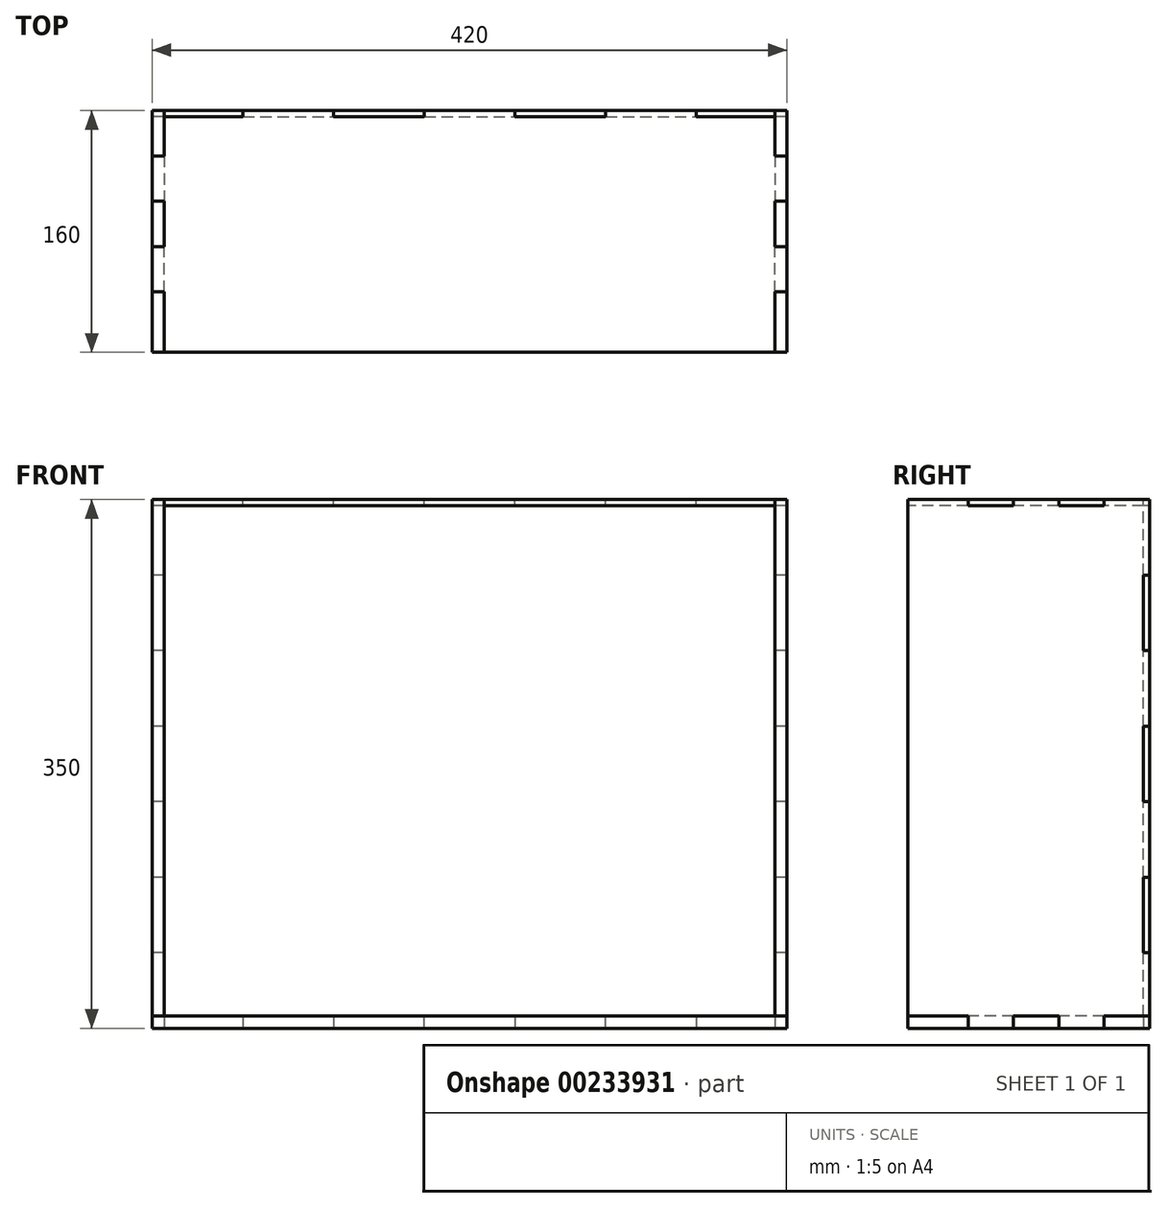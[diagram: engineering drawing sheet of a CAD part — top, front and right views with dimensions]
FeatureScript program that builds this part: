
annotation { "Feature Type Name" : "Feature", "Feature Type Description" : "" }
export const myFeature = defineFeature(function(context is Context, id is Id, definition is map)
    precondition{}
    {
        {
            var Q0;
            Q0=qCreatedBy(makeId("Top.planeOp"),FACE);
            var sketch = newSketch(context, id + "F0", { "sketchPlane" : qUnion([Q0])});
            skLineSegment(sketch, "E0", {"start": v(0, 0) * mm, "end": v(0, 40) * mm});
            skLineSegment(sketch, "E1", {"start": v(0, 40) * mm, "end": v(8, 40) * mm});
            skLineSegment(sketch, "E2", {"start": v(8, 40) * mm, "end": v(8, 70) * mm});
            skLineSegment(sketch, "E3", {"start": v(8, 70) * mm, "end": v(0, 70) * mm});
            skLineSegment(sketch, "E4", {"start": v(0, 70) * mm, "end": v(0, 100) * mm});
            skLineSegment(sketch, "E5", {"start": v(0, 100) * mm, "end": v(8, 100) * mm});
            skLineSegment(sketch, "E6", {"start": v(8, 100) * mm, "end": v(8, 130) * mm});
            skLineSegment(sketch, "E7", {"start": v(8, 130) * mm, "end": v(0, 130) * mm});
            skLineSegment(sketch, "E8", {"start": v(0, 130) * mm, "end": v(0, 160) * mm});
            skLineSegment(sketch, "E9", {"start": v(0, 160) * mm, "end": v(60, 160) * mm});
            skLineSegment(sketch, "E10", {"start": v(60, 160) * mm, "end": v(60, 156) * mm});
            skLineSegment(sketch, "E11", {"start": v(60, 156) * mm, "end": v(120, 156) * mm});
            skLineSegment(sketch, "E12", {"start": v(120, 156) * mm, "end": v(120, 160) * mm});
            skLineSegment(sketch, "E13", {"start": v(120, 160) * mm, "end": v(180, 160) * mm});
            skLineSegment(sketch, "E14", {"start": v(180, 160) * mm, "end": v(180, 156) * mm});
            skLineSegment(sketch, "E15", {"start": v(180, 156) * mm, "end": v(240, 156) * mm});
            skLineSegment(sketch, "E16", {"start": v(240, 156) * mm, "end": v(240, 160) * mm});
            skLineSegment(sketch, "E17", {"start": v(240, 160) * mm, "end": v(300, 160) * mm});
            skLineSegment(sketch, "E18", {"start": v(300, 160) * mm, "end": v(300, 156) * mm});
            skLineSegment(sketch, "E19", {"start": v(300, 156) * mm, "end": v(360, 156) * mm});
            skLineSegment(sketch, "E20", {"start": v(360, 156) * mm, "end": v(360, 160) * mm});
            skLineSegment(sketch, "E21", {"start": v(360, 160) * mm, "end": v(420, 160) * mm});
            skLineSegment(sketch, "E22", {"start": v(420, 160) * mm, "end": v(420, 130) * mm});
            skLineSegment(sketch, "E23", {"start": v(420, 130) * mm, "end": v(412, 130) * mm});
            skLineSegment(sketch, "E24", {"start": v(412, 130) * mm, "end": v(412, 100) * mm});
            skLineSegment(sketch, "E25", {"start": v(412, 100) * mm, "end": v(420, 100) * mm});
            skLineSegment(sketch, "E26", {"start": v(420, 100) * mm, "end": v(420, 70) * mm});
            skLineSegment(sketch, "E27", {"start": v(420, 70) * mm, "end": v(412, 70) * mm});
            skLineSegment(sketch, "E28", {"start": v(412, 70) * mm, "end": v(412, 40) * mm});
            skLineSegment(sketch, "E29", {"start": v(412, 40) * mm, "end": v(420, 40) * mm});
            skLineSegment(sketch, "E30", {"start": v(420, 40) * mm, "end": v(420, 0) * mm});
            skLineSegment(sketch, "E31", {"start": v(420, 0) * mm, "end": v(0, 0) * mm});
            skSolve(sketch);
        }
        {
            var Q0;
            Q0=makeQuery(id+"F0.imprint","IMPRINT",FACE,{"disambiguationData":[TD([[makeQuery(id+"F0.imprint","IMPRINT",EDGE,{"derivedFrom":sQuery(id+"F0.wireOp",EDGE,"E0")}),-1.0]])]});
            extrude(context, id + "F1", {"entities" : qUnion([Q0]), "depth" : 8 * mm});
        }
        {
            var Q0;
            Q0=makeQuery(id+"F1.opExtrude","SWEPT_FACE",FACE,{"disambiguationData":[OSD([sQuery(id+"F0.wireOp",EDGE,"E0")])]});
            var sketch = newSketch(context, id + "F2", { "sketchPlane" : qUnion([Q0])});
            skLineSegment(sketch, "E32", {"start": v(0, 8) * mm, "end": v(-40, 8) * mm});
            skLineSegment(sketch, "E33", {"start": v(-40, 8) * mm, "end": v(-40, 0) * mm});
            skLineSegment(sketch, "E34", {"start": v(-40, 0) * mm, "end": v(-70, 0) * mm});
            skLineSegment(sketch, "E35", {"start": v(-70, 0) * mm, "end": v(-70, 8) * mm});
            skLineSegment(sketch, "E36", {"start": v(-70, 8) * mm, "end": v(-100, 8) * mm});
            skLineSegment(sketch, "E37", {"start": v(-100, 8) * mm, "end": v(-100, 0) * mm});
            skLineSegment(sketch, "E38", {"start": v(-100, 0) * mm, "end": v(-130, 0) * mm});
            skLineSegment(sketch, "E39", {"start": v(-130, 0) * mm, "end": v(-130, 8) * mm});
            skLineSegment(sketch, "E40", {"start": v(-130, 8) * mm, "end": v(-160, 8) * mm});
            skLineSegment(sketch, "E41", {"start": v(-160, 8) * mm, "end": v(-160, 50) * mm});
            skLineSegment(sketch, "E42", {"start": v(-160, 50) * mm, "end": v(-156, 50) * mm});
            skLineSegment(sketch, "E43", {"start": v(-156, 50) * mm, "end": v(-156, 100) * mm});
            skLineSegment(sketch, "E44", {"start": v(-156, 100) * mm, "end": v(-160, 100) * mm});
            skLineSegment(sketch, "E45", {"start": v(-160, 100) * mm, "end": v(-160, 150) * mm});
            skLineSegment(sketch, "E46", {"start": v(-160, 150) * mm, "end": v(-156, 150) * mm});
            skLineSegment(sketch, "E47", {"start": v(-156, 150) * mm, "end": v(-156, 200) * mm});
            skLineSegment(sketch, "E48", {"start": v(-156, 200) * mm, "end": v(-160, 200) * mm});
            skLineSegment(sketch, "E49", {"start": v(-160, 200) * mm, "end": v(-160, 250) * mm});
            skLineSegment(sketch, "E50", {"start": v(-160, 250) * mm, "end": v(-156, 250) * mm});
            skLineSegment(sketch, "E51", {"start": v(-156, 250) * mm, "end": v(-156, 300) * mm});
            skLineSegment(sketch, "E52", {"start": v(-156, 300) * mm, "end": v(-160, 300) * mm});
            skLineSegment(sketch, "E53", {"start": v(-160, 300) * mm, "end": v(-160, 350) * mm});
            skLineSegment(sketch, "E54", {"start": v(-160, 350) * mm, "end": v(-130, 350) * mm});
            skLineSegment(sketch, "E55", {"start": v(-130, 350) * mm, "end": v(-130, 346) * mm});
            skLineSegment(sketch, "E56", {"start": v(-130, 346) * mm, "end": v(-100, 346) * mm});
            skLineSegment(sketch, "E57", {"start": v(-100, 346) * mm, "end": v(-100, 350) * mm});
            skLineSegment(sketch, "E58", {"start": v(-100, 350) * mm, "end": v(-70, 350) * mm});
            skLineSegment(sketch, "E59", {"start": v(-70, 350) * mm, "end": v(-70, 346) * mm});
            skLineSegment(sketch, "E60", {"start": v(-70, 346) * mm, "end": v(-40, 346) * mm});
            skLineSegment(sketch, "E61", {"start": v(-40, 346) * mm, "end": v(-40, 350) * mm});
            skLineSegment(sketch, "E62", {"start": v(-40, 350) * mm, "end": v(0, 350) * mm});
            skLineSegment(sketch, "E63", {"start": v(0, 350) * mm, "end": v(0, 8) * mm});
            skSolve(sketch);
        }
        {
            var Q0;
            Q0 = qSketchRegion(id + "F2", true);
            extrude(context, id + "F3", {"entities" : qUnion([Q0]), "oppositeDirection" : true, "depth" : 8 * mm});
        }
        {
            var Q0;
            Q0=makeQuery(id+"F3.opExtrude","SWEPT_BODY",BODY,{"disambiguationData":[OSD([sQuery(id+"F2.wireOp",EDGE,"E32"),sQuery(id+"F2.wireOp",EDGE,"E33"),sQuery(id+"F2.wireOp",EDGE,"E34"),sQuery(id+"F2.wireOp",EDGE,"E35"),sQuery(id+"F2.wireOp",EDGE,"E36"),sQuery(id+"F2.wireOp",EDGE,"E37"),sQuery(id+"F2.wireOp",EDGE,"E38"),sQuery(id+"F2.wireOp",EDGE,"E39"),sQuery(id+"F2.wireOp",EDGE,"E40"),sQuery(id+"F2.wireOp",EDGE,"E41"),sQuery(id+"F2.wireOp",EDGE,"E42"),sQuery(id+"F2.wireOp",EDGE,"E43"),sQuery(id+"F2.wireOp",EDGE,"E44"),sQuery(id+"F2.wireOp",EDGE,"E45"),sQuery(id+"F2.wireOp",EDGE,"E46"),sQuery(id+"F2.wireOp",EDGE,"E47"),sQuery(id+"F2.wireOp",EDGE,"E48"),sQuery(id+"F2.wireOp",EDGE,"E49"),sQuery(id+"F2.wireOp",EDGE,"E50"),sQuery(id+"F2.wireOp",EDGE,"E51"),sQuery(id+"F2.wireOp",EDGE,"E52"),sQuery(id+"F2.wireOp",EDGE,"E53"),sQuery(id+"F2.wireOp",EDGE,"E54"),sQuery(id+"F2.wireOp",EDGE,"E55"),sQuery(id+"F2.wireOp",EDGE,"E56"),sQuery(id+"F2.wireOp",EDGE,"E57"),sQuery(id+"F2.wireOp",EDGE,"E58"),sQuery(id+"F2.wireOp",EDGE,"E59"),sQuery(id+"F2.wireOp",EDGE,"E60"),sQuery(id+"F2.wireOp",EDGE,"E61"),sQuery(id+"F2.wireOp",EDGE,"E62"),sQuery(id+"F2.wireOp",EDGE,"E63")])]});
            var Q1;
            Q1=makeQuery(id+"F3.opExtrude","CAP_VERTEX",VERTEX,{"disambiguationData":[OSD([sQuery(id+"F0.wireOp",EDGE,"E0"),sQuery(id+"F0.wireOp",EDGE,"E31"),sQuery(id+"F2.wireOp",EDGE,"E32"),sQuery(id+"F2.wireOp",EDGE,"E63")])],"isStart":false});
            var Q2;
            Q2=makeQuery(id+"F1.opExtrude","CAP_VERTEX",VERTEX,{"disambiguationData":[OSD([sQuery(id+"F0.wireOp",EDGE,"E30"),sQuery(id+"F0.wireOp",EDGE,"E31")])],"isStart":false});
            transform(context, id + "F4", {"entities" : qUnion([Q0]), "transformType" : TransformType.TRANSLATION_ENTITY, "oppositeDirectionEntity" : false, "transformLine" : qUnion([Q1, Q2]), "makeCopy" : true});
        }
        {
            var Q0;
            Q0=makeQuery(id+"F1.opExtrude","SWEPT_FACE",FACE,{"disambiguationData":[OSD([sQuery(id+"F0.wireOp",EDGE,"E9")])]});
            var sketch = newSketch(context, id + "F5", { "sketchPlane" : qUnion([Q0])});
            skLineSegment(sketch, "E64", {"start": v(-60, 8) * mm, "end": v(-8, 8) * mm});
            skLineSegment(sketch, "E65", {"start": v(-8, 8) * mm, "end": v(-8, 50) * mm});
            skLineSegment(sketch, "E66", {"start": v(-8, 50) * mm, "end": v(0, 50) * mm});
            skLineSegment(sketch, "E67", {"start": v(0, 50) * mm, "end": v(0, 100) * mm});
            skLineSegment(sketch, "E68", {"start": v(0, 100) * mm, "end": v(-8, 100) * mm});
            skLineSegment(sketch, "E69", {"start": v(-8, 100) * mm, "end": v(-8, 150) * mm});
            skLineSegment(sketch, "E70", {"start": v(-8, 150) * mm, "end": v(0, 150) * mm});
            skLineSegment(sketch, "E71", {"start": v(0, 150) * mm, "end": v(0, 200) * mm});
            skLineSegment(sketch, "E72", {"start": v(0, 200) * mm, "end": v(-8, 200) * mm});
            skLineSegment(sketch, "E73", {"start": v(-8, 200) * mm, "end": v(-8, 250) * mm});
            skLineSegment(sketch, "E74", {"start": v(-8, 250) * mm, "end": v(0, 250) * mm});
            skLineSegment(sketch, "E75", {"start": v(0, 250) * mm, "end": v(0, 300) * mm});
            skLineSegment(sketch, "E76", {"start": v(0, 300) * mm, "end": v(-8, 300) * mm});
            skLineSegment(sketch, "E77", {"start": v(-8, 300) * mm, "end": v(-8, 350) * mm});
            skLineSegment(sketch, "E78", {"start": v(-8, 350) * mm, "end": v(-60, 350) * mm});
            skLineSegment(sketch, "E79", {"start": v(-60, 350) * mm, "end": v(-60, 346) * mm});
            skLineSegment(sketch, "E80", {"start": v(-60, 346) * mm, "end": v(-120, 346) * mm});
            skLineSegment(sketch, "E81", {"start": v(-120, 346) * mm, "end": v(-120, 350) * mm});
            skLineSegment(sketch, "E82", {"start": v(-120, 350) * mm, "end": v(-180, 350) * mm});
            skLineSegment(sketch, "E83", {"start": v(-180, 350) * mm, "end": v(-180, 346) * mm});
            skLineSegment(sketch, "E84", {"start": v(-180, 346) * mm, "end": v(-240, 346) * mm});
            skLineSegment(sketch, "E85", {"start": v(-240, 346) * mm, "end": v(-240, 350) * mm});
            skLineSegment(sketch, "E86", {"start": v(-240, 350) * mm, "end": v(-300, 350) * mm});
            skLineSegment(sketch, "E87", {"start": v(-300, 350) * mm, "end": v(-300, 346) * mm});
            skLineSegment(sketch, "E88", {"start": v(-300, 346) * mm, "end": v(-360, 346) * mm});
            skLineSegment(sketch, "E89", {"start": v(-360, 346) * mm, "end": v(-360, 350) * mm});
            skLineSegment(sketch, "E90", {"start": v(-360, 350) * mm, "end": v(-412, 350) * mm});
            skLineSegment(sketch, "E91", {"start": v(-412, 350) * mm, "end": v(-412, 300) * mm});
            skLineSegment(sketch, "E92", {"start": v(-412, 300) * mm, "end": v(-420, 300) * mm});
            skLineSegment(sketch, "E93", {"start": v(-420, 300) * mm, "end": v(-420, 250) * mm});
            skLineSegment(sketch, "E94", {"start": v(-420, 250) * mm, "end": v(-412, 250) * mm});
            skLineSegment(sketch, "E95", {"start": v(-412, 250) * mm, "end": v(-412, 200) * mm});
            skLineSegment(sketch, "E96", {"start": v(-412, 200) * mm, "end": v(-420, 200) * mm});
            skLineSegment(sketch, "E97", {"start": v(-420, 200) * mm, "end": v(-420, 150) * mm});
            skLineSegment(sketch, "E98", {"start": v(-420, 150) * mm, "end": v(-412, 150) * mm});
            skLineSegment(sketch, "E99", {"start": v(-412, 150) * mm, "end": v(-412, 100) * mm});
            skLineSegment(sketch, "E100", {"start": v(-412, 100) * mm, "end": v(-420, 100) * mm});
            skLineSegment(sketch, "E101", {"start": v(-420, 100) * mm, "end": v(-420, 50) * mm});
            skLineSegment(sketch, "E102", {"start": v(-420, 50) * mm, "end": v(-412, 50) * mm});
            skLineSegment(sketch, "E103", {"start": v(-412, 50) * mm, "end": v(-412, 8) * mm});
            skLineSegment(sketch, "E104", {"start": v(-412, 8) * mm, "end": v(-360, 8) * mm});
            skLineSegment(sketch, "E105", {"start": v(-360, 8) * mm, "end": v(-360, 0) * mm});
            skLineSegment(sketch, "E106", {"start": v(-360, 0) * mm, "end": v(-300, 0) * mm});
            skLineSegment(sketch, "E107", {"start": v(-300, 0) * mm, "end": v(-300, 8) * mm});
            skLineSegment(sketch, "E108", {"start": v(-300, 8) * mm, "end": v(-240, 8) * mm});
            skLineSegment(sketch, "E109", {"start": v(-240, 8) * mm, "end": v(-240, 0) * mm});
            skLineSegment(sketch, "E110", {"start": v(-240, 0) * mm, "end": v(-180, 0) * mm});
            skLineSegment(sketch, "E111", {"start": v(-180, 0) * mm, "end": v(-180, 8) * mm});
            skLineSegment(sketch, "E112", {"start": v(-180, 8) * mm, "end": v(-120, 8) * mm});
            skLineSegment(sketch, "E113", {"start": v(-120, 8) * mm, "end": v(-120, 0) * mm});
            skLineSegment(sketch, "E114", {"start": v(-120, 0) * mm, "end": v(-60, 0) * mm});
            skLineSegment(sketch, "E115", {"start": v(-60, 0) * mm, "end": v(-60, 8) * mm});
            skSolve(sketch);
        }
        {
            var Q0;
            Q0=makeQuery(id+"F5.imprint","IMPRINT",FACE,{"disambiguationData":[TD([[makeQuery(id+"F5.imprint","IMPRINT",EDGE,{"derivedFrom":sQuery(id+"F5.wireOp",EDGE,"E64")}),-1.0]])]});
            extrude(context, id + "F6", {"entities" : qUnion([Q0]), "oppositeDirection" : true, "depth" : 4 * mm});
        }
        {
            var Q0;
            Q0=makeQuery(id+"F3.opExtrude","SWEPT_FACE",FACE,{"disambiguationData":[OSD([sQuery(id+"F2.wireOp",EDGE,"E62")])]});
            var sketch = newSketch(context, id + "F7", { "sketchPlane" : qUnion([Q0])});
            skLineSegment(sketch, "E116", {"start": v(8, 0) * mm, "end": v(8, 40) * mm});
            skLineSegment(sketch, "E117", {"start": v(8, 40) * mm, "end": v(0, 40) * mm});
            skLineSegment(sketch, "E118", {"start": v(0, 40) * mm, "end": v(0, 70) * mm});
            skLineSegment(sketch, "E119", {"start": v(0, 70) * mm, "end": v(8, 70) * mm});
            skLineSegment(sketch, "E120", {"start": v(8, 70) * mm, "end": v(8, 100) * mm});
            skLineSegment(sketch, "E121", {"start": v(8, 100) * mm, "end": v(0, 100) * mm});
            skLineSegment(sketch, "E122", {"start": v(0, 100) * mm, "end": v(0, 130) * mm});
            skLineSegment(sketch, "E123", {"start": v(0, 130) * mm, "end": v(8, 130) * mm});
            skLineSegment(sketch, "E124", {"start": v(8, 130) * mm, "end": v(8, 156) * mm});
            skLineSegment(sketch, "E125", {"start": v(8, 156) * mm, "end": v(60, 156) * mm});
            skLineSegment(sketch, "E126", {"start": v(60, 156) * mm, "end": v(60, 160) * mm});
            skLineSegment(sketch, "E127", {"start": v(60, 160) * mm, "end": v(120, 160) * mm});
            skLineSegment(sketch, "E128", {"start": v(120, 160) * mm, "end": v(120, 156) * mm});
            skLineSegment(sketch, "E129", {"start": v(120, 156) * mm, "end": v(180, 156) * mm});
            skLineSegment(sketch, "E130", {"start": v(180, 156) * mm, "end": v(180, 160) * mm});
            skLineSegment(sketch, "E131", {"start": v(180, 160) * mm, "end": v(240, 160) * mm});
            skLineSegment(sketch, "E132", {"start": v(240, 160) * mm, "end": v(240, 156) * mm});
            skLineSegment(sketch, "E133", {"start": v(240, 156) * mm, "end": v(300, 156) * mm});
            skLineSegment(sketch, "E134", {"start": v(300, 156) * mm, "end": v(300, 160) * mm});
            skLineSegment(sketch, "E135", {"start": v(300, 160) * mm, "end": v(360, 160) * mm});
            skLineSegment(sketch, "E136", {"start": v(360, 160) * mm, "end": v(360, 156) * mm});
            skLineSegment(sketch, "E137", {"start": v(360, 156) * mm, "end": v(412, 156) * mm});
            skLineSegment(sketch, "E138", {"start": v(412, 156) * mm, "end": v(412, 130) * mm});
            skLineSegment(sketch, "E139", {"start": v(412, 130) * mm, "end": v(420, 130) * mm});
            skLineSegment(sketch, "E140", {"start": v(420, 130) * mm, "end": v(420, 100) * mm});
            skLineSegment(sketch, "E141", {"start": v(420, 100) * mm, "end": v(412, 100) * mm});
            skLineSegment(sketch, "E142", {"start": v(412, 100) * mm, "end": v(412, 70) * mm});
            skLineSegment(sketch, "E143", {"start": v(412, 70) * mm, "end": v(420, 70) * mm});
            skLineSegment(sketch, "E144", {"start": v(420, 70) * mm, "end": v(420, 40) * mm});
            skLineSegment(sketch, "E145", {"start": v(420, 40) * mm, "end": v(412, 40) * mm});
            skLineSegment(sketch, "E146", {"start": v(412, 40) * mm, "end": v(412, 0) * mm});
            skLineSegment(sketch, "E147", {"start": v(412, 0) * mm, "end": v(8, 0) * mm});
            skSolve(sketch);
        }
        {
            var Q0;
            Q0=makeQuery(id+"F7.imprint","IMPRINT",FACE,{"disambiguationData":[TD([[makeQuery(id+"F7.imprint","IMPRINT",EDGE,{"derivedFrom":sQuery(id+"F7.wireOp",EDGE,"E116")}),1.0]])]});
            extrude(context, id + "F8", {"entities" : qUnion([Q0]), "oppositeDirection" : true, "depth" : 4 * mm});
        }
    });
